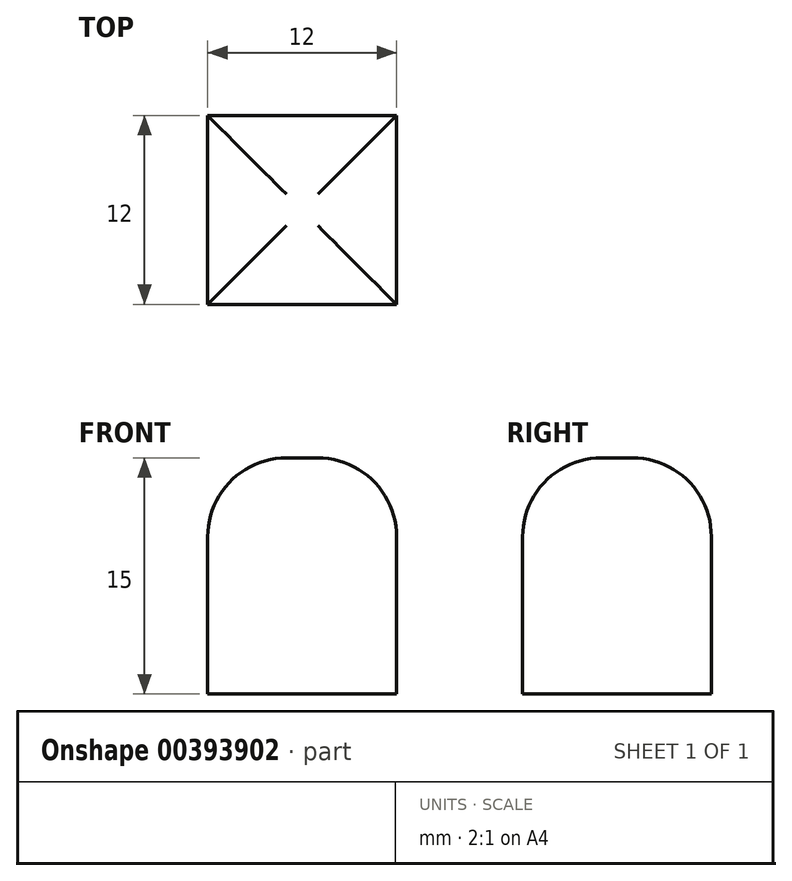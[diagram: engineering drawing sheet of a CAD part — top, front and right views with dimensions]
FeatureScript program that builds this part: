
annotation { "Feature Type Name" : "Feature", "Feature Type Description" : "" }
export const myFeature = defineFeature(function(context is Context, id is Id, definition is map)
    precondition{}
    {
        {
            var Q0;
            Q0=qCreatedBy(makeId("Top.planeOp"),FACE);
            var sketch = newSketch(context, id + "F0", { "sketchPlane" : qUnion([Q0])});
            skLineSegment(sketch, "E0.bottom", {"start": v(6, 6) * mm, "end": v(-6, 6) * mm});
            skLineSegment(sketch, "E0.top", {"start": v(6, -6) * mm, "end": v(-6, -6) * mm});
            skLineSegment(sketch, "E0.left", {"start": v(6, 6) * mm, "end": v(6, -6) * mm});
            skLineSegment(sketch, "E0.right", {"start": v(-6, 6) * mm, "end": v(-6, -6) * mm});
            skPoint(sketch, "E0.middle", {"position": v(0, 0) * mm});
            skSolve(sketch);
        }
        {
            var Q0;
            Q0=makeQuery(id+"F0.imprint","IMPRINT",FACE,{"disambiguationData":[TD([[makeQuery(id+"F0.imprint","IMPRINT",EDGE,{"derivedFrom":sQuery(id+"F0.wireOp",EDGE,"E0.bottom")}),1.0]])]});
            extrude(context, id + "F1", {"entities" : qUnion([Q0]), "depth" : 15 * mm, "offsetDistance" : 25 * mm});
        }
        {
            var Q0;
            Q0=makeQuery(id+"F1.opExtrude","CAP_FACE",FACE,{"disambiguationData":[OSD([sQuery(id+"F0.wireOp",EDGE,"E0.bottom"),sQuery(id+"F0.wireOp",EDGE,"E0.top"),sQuery(id+"F0.wireOp",EDGE,"E0.left"),sQuery(id+"F0.wireOp",EDGE,"E0.right")])],"isStart":false});
            fillet(context, id + "F2", {"entities" : qUnion([Q0]), "radius" : 5 * mm, "tangentPropagation" : true, "allowEdgeOverflow" : false});
        }
    });
